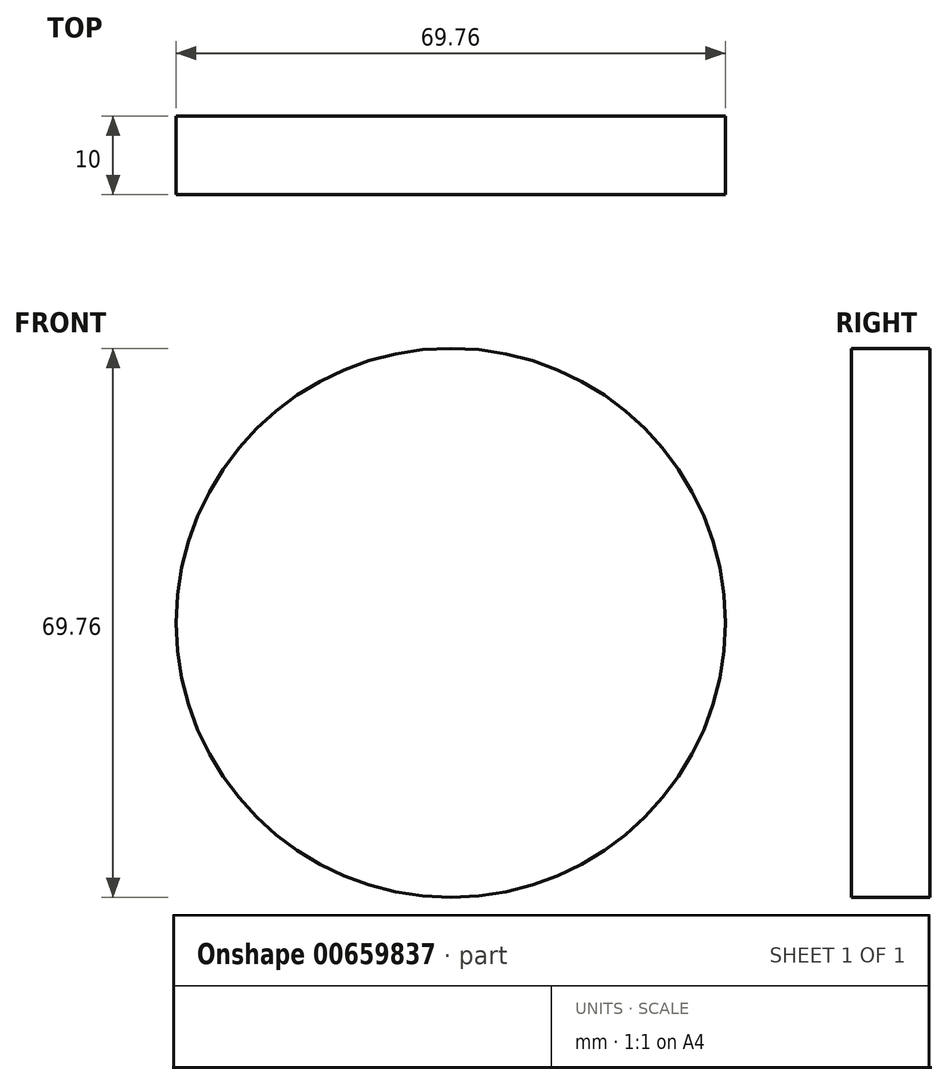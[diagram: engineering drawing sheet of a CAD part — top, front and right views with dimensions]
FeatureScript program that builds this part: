
annotation { "Feature Type Name" : "Feature", "Feature Type Description" : "" }
export const myFeature = defineFeature(function(context is Context, id is Id, definition is map)
    precondition{}
    {
        {
            var Q0;
            Q0=qCreatedBy(makeId("Front.planeOp"),FACE);
            var sketch = newSketch(context, id + "F0", { "sketchPlane" : qUnion([Q0])});
            skCircle(sketch, "E0", {"center": v(0, 0) * mm, "radius": 34.88 * mm});
            skSolve(sketch);
        }
        {
            var Q0;
            Q0 = qSketchRegion(id + "F0", true);
            extrude(context, id + "F1", {"entities" : qUnion([Q0]), "depth" : 10 * mm, "offsetDistance" : 25 * mm});
        }
    });
